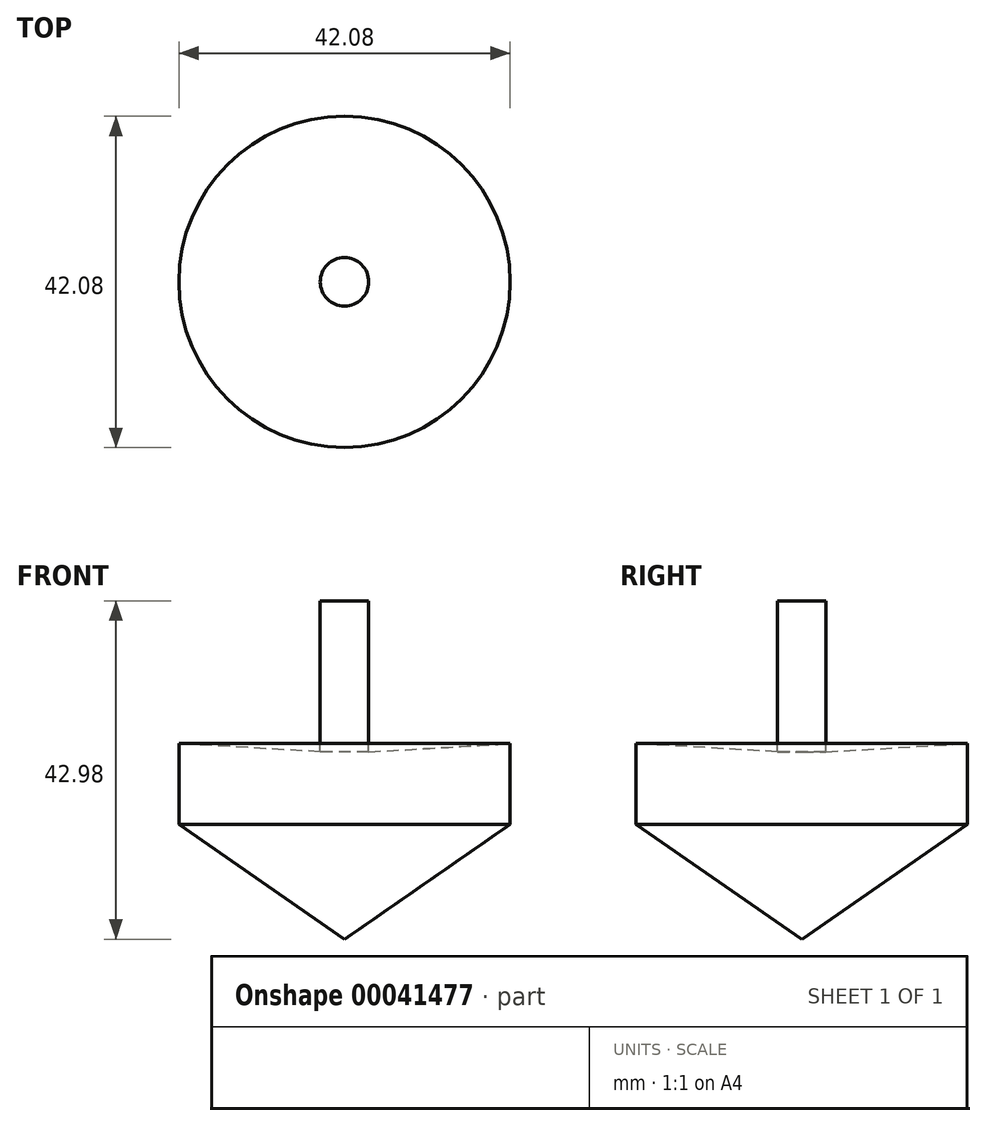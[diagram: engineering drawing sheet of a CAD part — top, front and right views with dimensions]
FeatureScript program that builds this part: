
annotation { "Feature Type Name" : "Feature", "Feature Type Description" : "" }
export const myFeature = defineFeature(function(context is Context, id is Id, definition is map)
    precondition{}
    {
        {
            var Q0;
            Q0=qCreatedBy(makeId("Front.planeOp"),FACE);
            var sketch = newSketch(context, id + "F0", { "sketchPlane" : qUnion([Q0])});
            skLineSegment(sketch, "E0", {"start": v(0, 22.37) * mm, "end": v(0, -20.6) * mm});
            skLineSegment(sketch, "E1", {"start": v(0, -20.6) * mm, "end": v(-21.04, -5.99) * mm});
            skLineSegment(sketch, "E2", {"start": v(-21.04, -5.99) * mm, "end": v(-21.04, 4.24) * mm});
            skLineSegment(sketch, "E3", {"start": v(0, 22.37) * mm, "end": v(-3.08, 22.37) * mm});
            skLineSegment(sketch, "E4", {"start": v(-3.08, 22.37) * mm, "end": v(-3.08, 3.2) * mm});
            skLineSegment(sketch, "E5", {"start": v(-3.08, 3.2) * mm, "end": v(-21.04, 4.24) * mm});
            skSolve(sketch);
        }
        {
            var Q0;
            Q0 = qSketchRegion(id + "F0", true);
            var Q1;
            Q1=sQuery(id+"F0.wireOp",EDGE,"E0");
            revolve(context, id + "F1", {"entities" : qUnion([Q0]), "axis" : qUnion([Q1]), "revolveType" : RevolveType.FULL});
        }
    });
